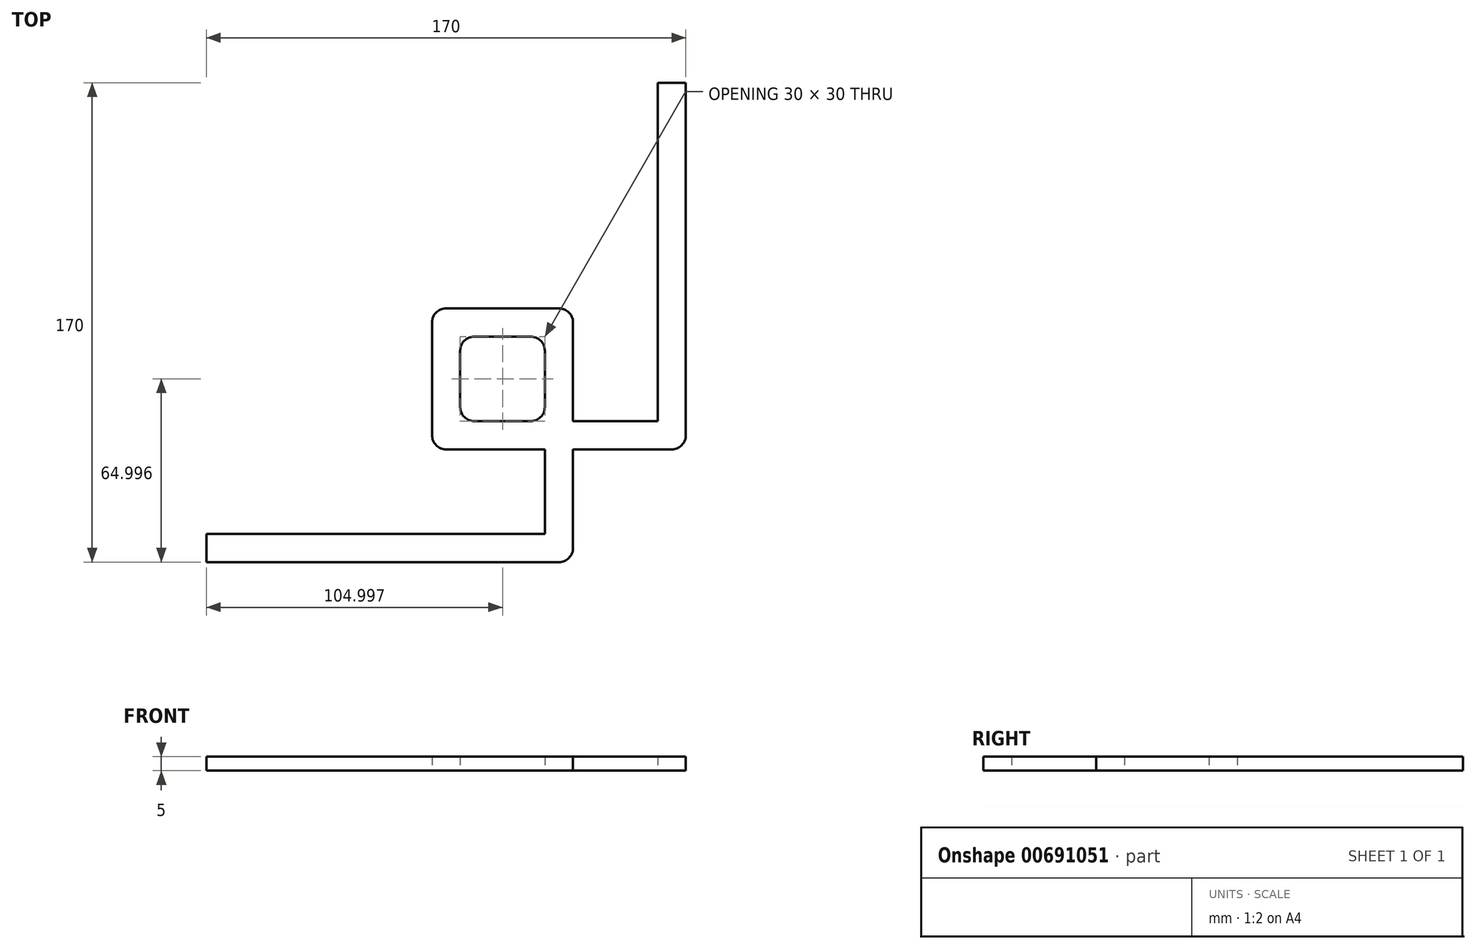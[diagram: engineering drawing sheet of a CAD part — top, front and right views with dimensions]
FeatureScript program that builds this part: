
annotation { "Feature Type Name" : "Feature", "Feature Type Description" : "" }
export const myFeature = defineFeature(function(context is Context, id is Id, definition is map)
    precondition{}
    {
        {
            var Q0;
            Q0=qCreatedBy(makeId("Top.planeOp"),FACE);
            var sketch = newSketch(context, id + "F0", { "sketchPlane" : qUnion([Q0])});
            skLineSegment(sketch, "E0.bottom", {"start": v(-8, 21.48) * mm, "end": v(12, 21.48) * mm});
            skLineSegment(sketch, "E0.top", {"start": v(-8, -8.52) * mm, "end": v(12, -8.52) * mm});
            skLineSegment(sketch, "E0.left", {"start": v(-13, 16.48) * mm, "end": v(-13, -3.52) * mm});
            skLineSegment(sketch, "E0.right", {"start": v(17, 16.48) * mm, "end": v(17, -3.52) * mm});
            skLineSegment(sketch, "E1.bottom", {"start": v(-18, 31.48) * mm, "end": v(22, 31.48) * mm});
            skLineSegment(sketch, "E1.top", {"start": v(-18, -18.52) * mm, "end": v(27, -18.52) * mm});
            skLineSegment(sketch, "E1.left", {"start": v(-23, 26.48) * mm, "end": v(-23, -13.52) * mm});
            skLineSegment(sketch, "E1.right", {"start": v(27, 26.48) * mm, "end": v(27, -18.52) * mm});
            skLineSegment(sketch, "E2", {"start": v(17, -18.52) * mm, "end": v(17, -48.52) * mm});
            skLineSegment(sketch, "E3", {"start": v(17, -48.52) * mm, "end": v(-103, -48.52) * mm});
            skLineSegment(sketch, "E4", {"start": v(-103, -48.52) * mm, "end": v(-103, -58.52) * mm});
            skLineSegment(sketch, "E5", {"start": v(-103, -58.52) * mm, "end": v(22, -58.52) * mm});
            skLineSegment(sketch, "E6", {"start": v(27, -53.52) * mm, "end": v(27, -18.52) * mm});
            skLineSegment(sketch, "E7", {"start": v(27, -8.52) * mm, "end": v(57, -8.52) * mm});
            skLineSegment(sketch, "E8", {"start": v(57, -8.52) * mm, "end": v(57, 111.48) * mm});
            skLineSegment(sketch, "E9", {"start": v(27, -18.52) * mm, "end": v(62, -18.52) * mm});
            skLineSegment(sketch, "E10", {"start": v(67, -13.52) * mm, "end": v(67, 111.48) * mm});
            skLineSegment(sketch, "E11", {"start": v(67, 111.48) * mm, "end": v(57, 111.48) * mm});
            skPoint(sketch, "E12.visualSharp", {"position": v(-23, 31.48) * mm});
            skArc(sketch, "E12.filletArc", {"start": v(-18, 31.48) * mm, "mid": v(-21.53, 30.01) * mm, "end": v(-23, 26.48) * mm});
            skPoint(sketch, "E13.visualSharp", {"position": v(27, 31.48) * mm});
            skArc(sketch, "E13.filletArc", {"start": v(27, 26.48) * mm, "mid": v(25.54, 30.01) * mm, "end": v(22, 31.48) * mm});
            skPoint(sketch, "E14.visualSharp", {"position": v(-13, 21.48) * mm});
            skArc(sketch, "E14.filletArc", {"start": v(-8, 21.48) * mm, "mid": v(-11.53, 20.01) * mm, "end": v(-13, 16.48) * mm});
            skPoint(sketch, "E15.visualSharp", {"position": v(17, 21.48) * mm});
            skArc(sketch, "E15.filletArc", {"start": v(17, 16.48) * mm, "mid": v(15.54, 20.01) * mm, "end": v(12, 21.48) * mm});
            skPoint(sketch, "E16.visualSharp", {"position": v(-23, -18.52) * mm});
            skArc(sketch, "E16.filletArc", {"start": v(-23, -13.52) * mm, "mid": v(-21.53, -17.06) * mm, "end": v(-18, -18.52) * mm});
            skPoint(sketch, "E17.visualSharp", {"position": v(-13, -8.52) * mm});
            skArc(sketch, "E17.filletArc", {"start": v(-13, -3.52) * mm, "mid": v(-11.53, -7.06) * mm, "end": v(-8, -8.52) * mm});
            skPoint(sketch, "E18.visualSharp", {"position": v(17, -8.52) * mm});
            skArc(sketch, "E18.filletArc", {"start": v(12, -8.52) * mm, "mid": v(15.54, -7.06) * mm, "end": v(17, -3.52) * mm});
            skPoint(sketch, "E19.visualSharp", {"position": v(67, -18.52) * mm});
            skArc(sketch, "E19.filletArc", {"start": v(62, -18.52) * mm, "mid": v(65.54, -17.06) * mm, "end": v(67, -13.52) * mm});
            skPoint(sketch, "E20.visualSharp", {"position": v(27, -58.52) * mm});
            skArc(sketch, "E20.filletArc", {"start": v(22, -58.52) * mm, "mid": v(25.54, -57.06) * mm, "end": v(27, -53.52) * mm});
            skSolve(sketch);
        }
        {
            var Q0;
            Q0=makeQuery(id+"F0.imprint","IMPRINT",FACE,{"disambiguationData":[TD([[makeQuery(id+"F0.imprint","IMPRINT",EDGE,{"derivedFrom":sQuery(id+"F0.wireOp",EDGE,"E0.bottom")}),1.0]])]});
            var Q1;
            {var subQ1=sQuery(id+"F0.wireOp",EDGE,"E7");Q1=makeQuery(id+"F0.imprint","IMPRINT",FACE,{"disambiguationData":[TD([[makeQuery(id+"F0.imprint","IMPRINT",EDGE,{"derivedFrom":subQ1}),-1.0]])]});}
            var Q2;
            {var subQ0=sQuery(id+"F0.wireOp",EDGE,"E2");Q2=makeQuery(id+"F0.imprint","IMPRINT",FACE,{"disambiguationData":[TD([[makeQuery(id+"F0.imprint","IMPRINT",EDGE,{"derivedFrom":subQ0}),1.0]])]});}
            extrude(context, id + "F1", {"entities" : qUnion([Q0, Q1, Q2]), "depth" : 5 * mm, "offsetDistance" : 25 * mm});
        }
    });
